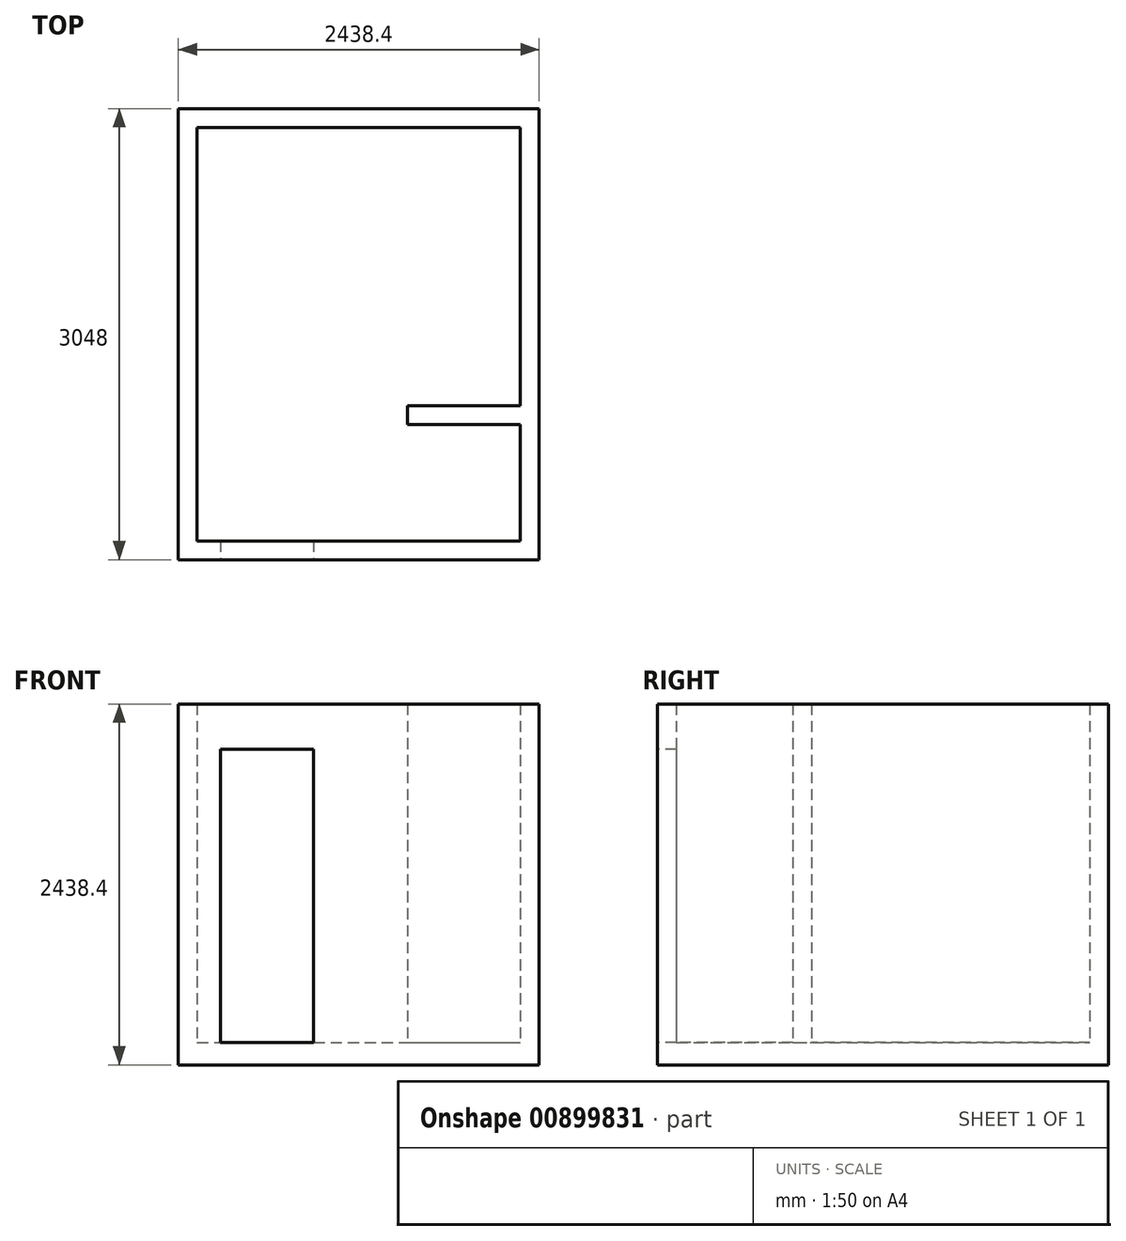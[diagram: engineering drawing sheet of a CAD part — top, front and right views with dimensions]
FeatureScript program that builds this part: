
annotation { "Feature Type Name" : "Feature", "Feature Type Description" : "" }
export const myFeature = defineFeature(function(context is Context, id is Id, definition is map)
    precondition{}
    {
        {
            var Q0;
            Q0=qCreatedBy(makeId("Top.planeOp"),FACE);
            var sketch = newSketch(context, id + "F0", { "sketchPlane" : qUnion([Q0])});
            skLineSegment(sketch, "E0", {"start": v(0, 0) * mm, "end": v(0, 3048) * mm});
            skLineSegment(sketch, "E1", {"start": v(0, 3048) * mm, "end": v(2438.4, 3048) * mm});
            skLineSegment(sketch, "E2", {"start": v(2438.4, 3048) * mm, "end": v(2438.4, 0) * mm});
            skLineSegment(sketch, "E3", {"start": v(2438.4, 0) * mm, "end": v(914.4, 0) * mm});
            skLineSegment(sketch, "E4", {"start": v(0, 0) * mm, "end": v(283.72, 0) * mm});
            skLineSegment(sketch, "E5.0", {"start": v(2311.4, 127) * mm, "end": v(914.4, 127) * mm});
            skLineSegment(sketch, "E5.1", {"start": v(127, 127) * mm, "end": v(283.72, 127) * mm});
            skLineSegment(sketch, "E5.2", {"start": v(127, 127) * mm, "end": v(127, 2921) * mm});
            skLineSegment(sketch, "E5.3", {"start": v(127, 2921) * mm, "end": v(2311.4, 2921) * mm});
            skLineSegment(sketch, "E5.4", {"start": v(2311.4, 2921) * mm, "end": v(2311.4, 1041.4) * mm});
            skLineSegment(sketch, "E6", {"start": v(283.72, 127) * mm, "end": v(283.72, 0) * mm});
            skLineSegment(sketch, "E7", {"start": v(914.4, 127) * mm, "end": v(914.4, 0) * mm});
            skLineSegment(sketch, "E8", {"start": v(2311.4, 914.4) * mm, "end": v(1549.4, 914.4) * mm});
            skLineSegment(sketch, "E9", {"start": v(1549.4, 914.4) * mm, "end": v(1549.4, 1041.4) * mm});
            skLineSegment(sketch, "E10", {"start": v(1549.4, 1041.4) * mm, "end": v(2311.4, 1041.4) * mm});
            skLineSegment(sketch, "E11.trimOffspring", {"start": v(2311.4, 914.4) * mm, "end": v(2311.4, 127) * mm});
            skSolve(sketch);
        }
        {
            var Q0;
            Q0 = qSketchRegion(id + "F0", true);
            extrude(context, id + "F1", {"entities" : qUnion([Q0]), "depth" : 2286 * mm, "offsetDistance" : 25.4 * mm});
        }
        {
            var Q0;
            Q0=makeQuery(id+"F1.opExtrude","CAP_FACE",FACE,{"disambiguationData":[OSD([sQuery(id+"F0.wireOp",EDGE,"E0"),sQuery(id+"F0.wireOp",EDGE,"E1"),sQuery(id+"F0.wireOp",EDGE,"E2"),sQuery(id+"F0.wireOp",EDGE,"E3"),sQuery(id+"F0.wireOp",EDGE,"E4"),sQuery(id+"F0.wireOp",EDGE,"E5.0"),sQuery(id+"F0.wireOp",EDGE,"E5.1"),sQuery(id+"F0.wireOp",EDGE,"E5.2"),sQuery(id+"F0.wireOp",EDGE,"E5.3"),sQuery(id+"F0.wireOp",EDGE,"E5.4"),sQuery(id+"F0.wireOp",EDGE,"E6"),sQuery(id+"F0.wireOp",EDGE,"E7"),sQuery(id+"F0.wireOp",EDGE,"E8"),sQuery(id+"F0.wireOp",EDGE,"E9"),sQuery(id+"F0.wireOp",EDGE,"E10"),sQuery(id+"F0.wireOp",EDGE,"E11.trimOffspring")])],"isStart":true});
            var sketch = newSketch(context, id + "F2", { "sketchPlane" : qUnion([Q0])});
            skLineSegment(sketch, "E12.bottom", {"start": v(0, 0) * mm, "end": v(2438.4, 0) * mm});
            skLineSegment(sketch, "E12.top", {"start": v(0, -3048) * mm, "end": v(2438.4, -3048) * mm});
            skLineSegment(sketch, "E12.left", {"start": v(0, 0) * mm, "end": v(0, -3048) * mm});
            skLineSegment(sketch, "E12.right", {"start": v(2438.4, 0) * mm, "end": v(2438.4, -3048) * mm});
            skSolve(sketch);
        }
        {
            var Q0;
            Q0 = qSketchRegion(id + "F2", true);
            extrude(context, id + "F3", {"entities" : qUnion([Q0]), "operationType" : NewBodyOperationType.ADD, "depth" : 152.4 * mm, "offsetDistance" : 25.4 * mm});
        }
        {
            var Q0;
            Q0=makeQuery(id+"F1.opExtrude","CAP_FACE",FACE,{"disambiguationData":[OSD([sQuery(id+"F0.wireOp",EDGE,"E0"),sQuery(id+"F0.wireOp",EDGE,"E1"),sQuery(id+"F0.wireOp",EDGE,"E2"),sQuery(id+"F0.wireOp",EDGE,"E3"),sQuery(id+"F0.wireOp",EDGE,"E4"),sQuery(id+"F0.wireOp",EDGE,"E5.0"),sQuery(id+"F0.wireOp",EDGE,"E5.1"),sQuery(id+"F0.wireOp",EDGE,"E5.2"),sQuery(id+"F0.wireOp",EDGE,"E5.3"),sQuery(id+"F0.wireOp",EDGE,"E5.4"),sQuery(id+"F0.wireOp",EDGE,"E6"),sQuery(id+"F0.wireOp",EDGE,"E7"),sQuery(id+"F0.wireOp",EDGE,"E8"),sQuery(id+"F0.wireOp",EDGE,"E9"),sQuery(id+"F0.wireOp",EDGE,"E10"),sQuery(id+"F0.wireOp",EDGE,"E11.trimOffspring")])],"isStart":false});
            var sketch = newSketch(context, id + "F4", { "sketchPlane" : qUnion([Q0])});
            skLineSegment(sketch, "E13.bottom", {"start": v(205.36, 127) * mm, "end": v(1045.7, 127) * mm});
            skLineSegment(sketch, "E13.top", {"start": v(205.36, 0) * mm, "end": v(1045.7, 0) * mm});
            skLineSegment(sketch, "E13.left", {"start": v(205.36, 127) * mm, "end": v(205.36, 0) * mm});
            skLineSegment(sketch, "E13.right", {"start": v(1045.7, 127) * mm, "end": v(1045.7, 0) * mm});
            skSolve(sketch);
        }
        {
            var Q0;
            Q0 = qSketchRegion(id + "F4", true);
            extrude(context, id + "F5", {"entities" : qUnion([Q0]), "operationType" : NewBodyOperationType.ADD, "oppositeDirection" : true, "depth" : 304.8 * mm, "offsetDistance" : 25.4 * mm});
        }
    });
